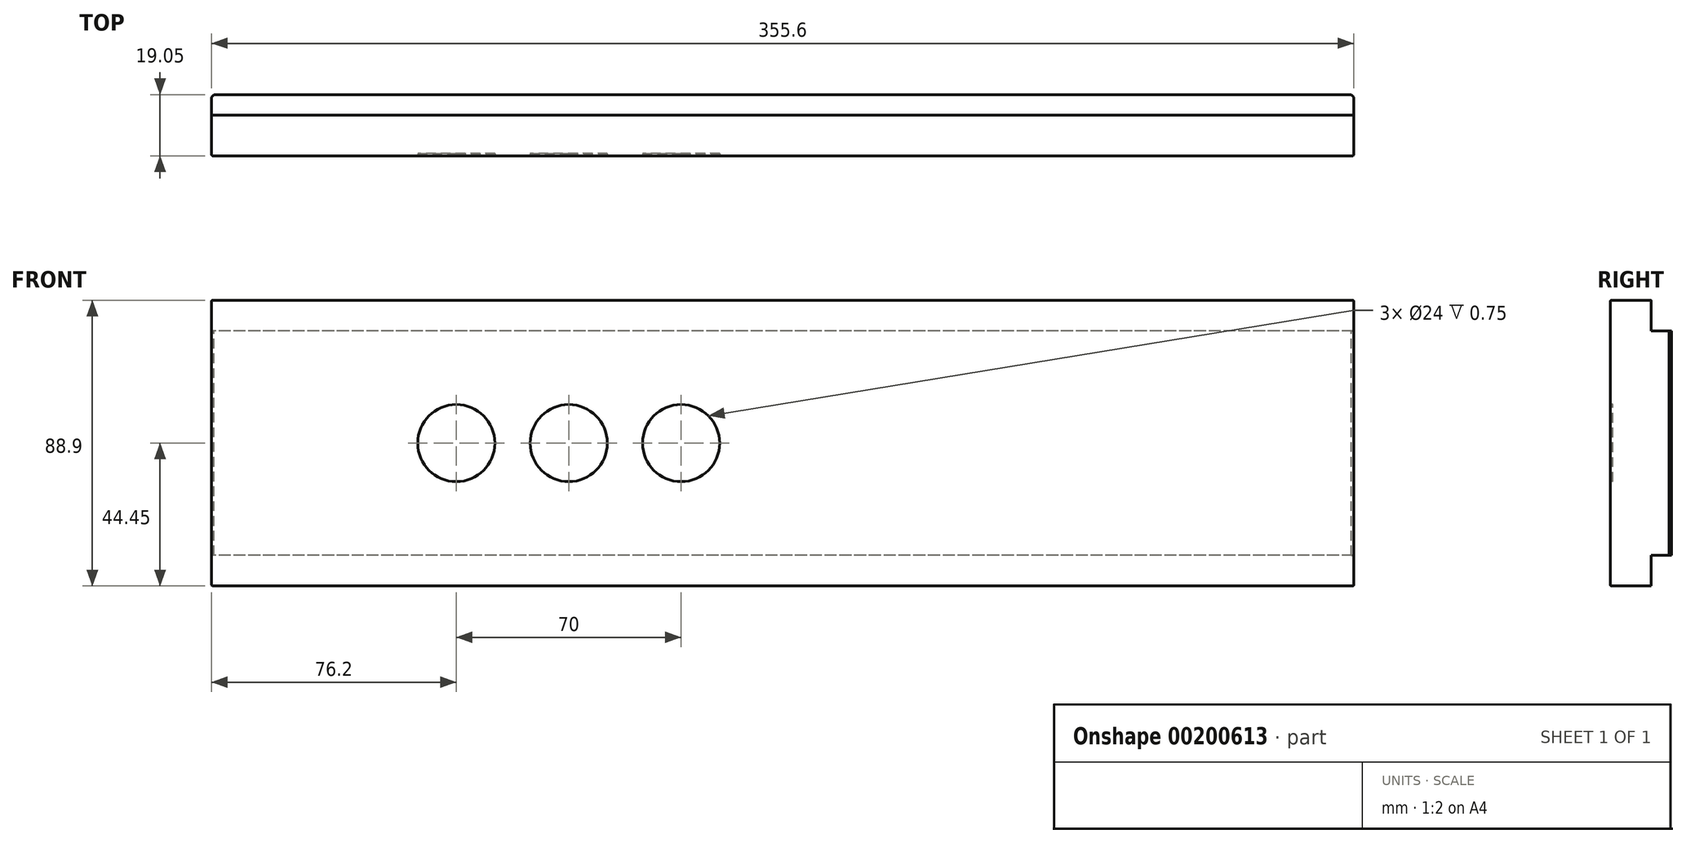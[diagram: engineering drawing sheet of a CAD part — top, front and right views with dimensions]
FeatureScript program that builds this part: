
annotation { "Feature Type Name" : "Feature", "Feature Type Description" : "" }
export const myFeature = defineFeature(function(context is Context, id is Id, definition is map)
    precondition{}
    {
        {
            assignVariable(context, id + "F0", {"name" : "width", "anyValue" : 0.75});
        }
        {
            var Q0;
            Q0=qCreatedBy(makeId("Right.planeOp"),FACE);
            var sketch = newSketch(context, id + "F1", { "sketchPlane" : qUnion([Q0])});
            skLineSegment(sketch, "E0.top", {"start": v(-6.35, 34.93) * mm, "end": v(0, 34.93) * mm});
            skLineSegment(sketch, "E0.left", {"start": v(-6.35, 44.45) * mm, "end": v(-6.35, 34.93) * mm});
            skLineSegment(sketch, "E1.bottom", {"start": v(0, 0) * mm, "end": v(-19.05, 0) * mm});
            skLineSegment(sketch, "E2", {"start": v(-19.05, 44.45) * mm, "end": v(-19.05, 0) * mm});
            skLineSegment(sketch, "E3", {"start": v(-19.05, 44.45) * mm, "end": v(-6.35, 44.45) * mm});
            skLineSegment(sketch, "E4", {"start": v(0, 34.93) * mm, "end": v(0, 0) * mm});
            skSolve(sketch);
        }
        {
            var Q0;
            Q0=makeQuery(id+"F1.imprint","IMPRINT",FACE,{"disambiguationData":[TD([[makeQuery(id+"F1.imprint","IMPRINT",EDGE,{"derivedFrom":sQuery(id+"F1.wireOp",EDGE,"E0.top")}),-1.0]])]});
            var Q1;
            Q1=makeQuery(id+"F1.imprint","IMPRINT",FACE,{"disambiguationData":[TD([[makeQuery(id+"F1.imprint","IMPRINT",EDGE,{"derivedFrom":sQuery(id+"F1.wireOp",EDGE,"E1.bottom")}),1.0]])]});
            extrude(context, id + "F2", {"entities" : qUnion([Q0, Q1]), "depth" : 177.8 * mm});
        }
        {
            var Q0;
            {var subQ0=makeQuery(id+"F4.opChamfer","BLEND_EDGE",EDGE,{"blendedFrom":[makeQuery(id+"F2.opExtrude","CAP_EDGE",EDGE,{"disambiguationData":[OSD([sQuery(id+"F1.wireOp",EDGE,"E4")])],"isStart":true}),makeQuery(id+"F2.opExtrude","SWEPT_FACE",FACE,{"disambiguationData":[OSD([sQuery(id+"F1.wireOp",EDGE,"E2")])]})],"blendedInto":[makeQuery(id+"F2.opExtrude","SWEPT_FACE",FACE,{"disambiguationData":[OSD([sQuery(id+"F1.wireOp",EDGE,"E2")])]})]});Q0=makeQuery(id+"F7.boolean.opBoolean","MERGE",EDGE,{"derivedFrom":[subQ0,makeQuery(id+"F7.opPattern","COPY",EDGE,{"derivedFrom":subQ0,"instanceName":"1"})]});}
            var Q1;
            Q1=makeQuery(id+"F2.opExtrude","CAP_EDGE",EDGE,{"disambiguationData":[OSD([sQuery(id+"F1.wireOp",EDGE,"E2")])],"isStart":true});
            fillet(context, id + "F3", {"entities" : qUnion([Q0, Q1]), "radius" : (getVariable(context, 'width') / 2) * mm, "tangentPropagation" : true, "allowEdgeOverflow" : false});
        }
        {
            var Q0;
            Q0=makeQuery(id+"F2.opExtrude","CAP_EDGE",EDGE,{"disambiguationData":[OSD([sQuery(id+"F1.wireOp",EDGE,"E4"),sQuery(id+"F1.wireOp",EDGE,"06acdf28-0093-4394-9228-6f8524038c1c4.MirrorCS")])],"isStart":true});
            chamfer(context, id + "F4", {"entities" : qUnion([Q0]), "width" : (getVariable(context, 'width')) * mm, "tangentPropagation" : true});
        }
        {
            var Q0;
            Q0=makeQuery(id+"F2.opExtrude","SWEPT_BODY",BODY,{"disambiguationData":[OSD([sQuery(id+"F1.wireOp",EDGE,"E0.top"),sQuery(id+"F1.wireOp",EDGE,"E0.left"),sQuery(id+"F1.wireOp",EDGE,"E2"),sQuery(id+"F1.wireOp",EDGE,"E3"),sQuery(id+"F1.wireOp",EDGE,"E4"),sQuery(id+"F1.wireOp",EDGE,"06acdf28-0093-4394-9228-6f8524038c1c0.MirrorCS"),sQuery(id+"F1.wireOp",EDGE,"06acdf28-0093-4394-9228-6f8524038c1c1.MirrorCS"),sQuery(id+"F1.wireOp",EDGE,"06acdf28-0093-4394-9228-6f8524038c1c2.MirrorCS"),sQuery(id+"F1.wireOp",EDGE,"06acdf28-0093-4394-9228-6f8524038c1c3.MirrorCS"),sQuery(id+"F1.wireOp",EDGE,"06acdf28-0093-4394-9228-6f8524038c1c4.MirrorCS")])]});
            var Q1;
            Q1=makeQuery(id+"F2.opExtrude","CAP_FACE",FACE,{"disambiguationData":[OSD([sQuery(id+"F1.wireOp",EDGE,"E0.top"),sQuery(id+"F1.wireOp",EDGE,"E0.left"),sQuery(id+"F1.wireOp",EDGE,"E2"),sQuery(id+"F1.wireOp",EDGE,"E3"),sQuery(id+"F1.wireOp",EDGE,"E4"),sQuery(id+"F1.wireOp",EDGE,"06acdf28-0093-4394-9228-6f8524038c1c0.MirrorCS"),sQuery(id+"F1.wireOp",EDGE,"06acdf28-0093-4394-9228-6f8524038c1c1.MirrorCS"),sQuery(id+"F1.wireOp",EDGE,"06acdf28-0093-4394-9228-6f8524038c1c2.MirrorCS"),sQuery(id+"F1.wireOp",EDGE,"06acdf28-0093-4394-9228-6f8524038c1c3.MirrorCS"),sQuery(id+"F1.wireOp",EDGE,"06acdf28-0093-4394-9228-6f8524038c1c4.MirrorCS")])],"isStart":false});
            mirror(context, id + "F5", {"operationType" : NewBodyOperationType.ADD, "entities" : qUnion([Q0]), "mirrorPlane" : qUnion([Q1])});
        }
        {
            var Q0;
            {var subQ0=makeQuery(id+"F2.opExtrude","SWEPT_EDGE",EDGE,{"disambiguationData":[OSD([sQuery(id+"F1.wireOp",EDGE,"E2"),sQuery(id+"F1.wireOp",EDGE,"E3")])]});Q0=makeQuery(id+"F5.boolean.opBoolean","MERGE",EDGE,{"derivedFrom":[subQ0,makeQuery(id+"F5.opPattern","COPY",EDGE,{"derivedFrom":subQ0,"instanceName":"1"})]});}
            fillet(context, id + "F6", {"entities" : qUnion([Q0]), "radius" : (getVariable(context, 'width') / 2) * mm, "tangentPropagation" : true, "allowEdgeOverflow" : false});
        }
        {
            var Q0;
            Q0=makeQuery(id+"F2.opExtrude","SWEPT_BODY",BODY,{"disambiguationData":[OSD([sQuery(id+"F1.wireOp",EDGE,"E0.top"),sQuery(id+"F1.wireOp",EDGE,"E0.left"),sQuery(id+"F1.wireOp",EDGE,"E1.bottom"),sQuery(id+"F1.wireOp",EDGE,"E2"),sQuery(id+"F1.wireOp",EDGE,"E3"),sQuery(id+"F1.wireOp",EDGE,"E4")])]});
            var Q1;
            {var subQ0=makeQuery(id+"F2.opExtrude","SWEPT_FACE",FACE,{"disambiguationData":[OSD([sQuery(id+"F1.wireOp",EDGE,"E1.bottom")])]});Q1=makeQuery(id+"F5.boolean.opBoolean","MERGE",FACE,{"derivedFrom":[subQ0,makeQuery(id+"F5.opPattern","COPY",FACE,{"derivedFrom":subQ0,"instanceName":"1"})]});}
            mirror(context, id + "F7", {"operationType" : NewBodyOperationType.ADD, "entities" : qUnion([Q0]), "mirrorPlane" : qUnion([Q1])});
        }
        {
            var Q0;
            {var subQ0=makeQuery(id+"F2.opExtrude","SWEPT_FACE",FACE,{"disambiguationData":[OSD([sQuery(id+"F1.wireOp",EDGE,"E2")])]});var subQ1=makeQuery(id+"F5.boolean.opBoolean","MERGE",FACE,{"derivedFrom":[subQ0,makeQuery(id+"F5.opPattern","COPY",FACE,{"derivedFrom":subQ0,"instanceName":"1"})]});Q0=makeQuery(id+"F7.boolean.opBoolean","MERGE",FACE,{"derivedFrom":[subQ1,makeQuery(id+"F7.opPattern","COPY",FACE,{"derivedFrom":subQ1,"instanceName":"1"})]});}
            var sketch = newSketch(context, id + "F8", { "sketchPlane" : qUnion([Q0])});
            skCircle(sketch, "E5", {"center": v(76.2, 0) * mm, "radius": 12 * mm});
            skCircle(sketch, "E6", {"center": v(111.2, 0) * mm, "radius": 12 * mm});
            skCircle(sketch, "E7", {"center": v(146.2, 0) * mm, "radius": 12 * mm});
            skSolve(sketch);
        }
        {
            var Q0;
            Q0=makeQuery(id+"F8.imprint","IMPRINT",FACE,{"disambiguationData":[TD([[makeQuery(id+"F8.imprint","IMPRINT",EDGE,{"derivedFrom":sQuery(id+"F8.wireOp",EDGE,"E5")}),1.0]])]});
            var Q1;
            Q1=makeQuery(id+"F8.imprint","IMPRINT",FACE,{"disambiguationData":[TD([[makeQuery(id+"F8.imprint","IMPRINT",EDGE,{"derivedFrom":sQuery(id+"F8.wireOp",EDGE,"E6")}),1.0]])]});
            var Q2;
            Q2=makeQuery(id+"F8.imprint","IMPRINT",FACE,{"disambiguationData":[TD([[makeQuery(id+"F8.imprint","IMPRINT",EDGE,{"derivedFrom":sQuery(id+"F8.wireOp",EDGE,"E7")}),1.0]])]});
            extrude(context, id + "F9", {"entities" : qUnion([Q0, Q1, Q2]), "operationType" : NewBodyOperationType.REMOVE, "oppositeDirection" : true, "depth" : (getVariable(context, 'width')) * mm});
        }
        {
            var Q0;
            {var subQ0=makeQuery(id+"F2.opExtrude","SWEPT_FACE",FACE,{"disambiguationData":[OSD([sQuery(id+"F1.wireOp",EDGE,"E4")])]});var subQ1=makeQuery(id+"F5.boolean.opBoolean","MERGE",FACE,{"derivedFrom":[subQ0,makeQuery(id+"F5.opPattern","COPY",FACE,{"derivedFrom":subQ0,"instanceName":"1"})]});Q0=makeQuery(id+"F7.boolean.opBoolean","MERGE",FACE,{"derivedFrom":[subQ1,makeQuery(id+"F7.opPattern","COPY",FACE,{"derivedFrom":subQ1,"instanceName":"1"})]});}
            var sketch = newSketch(context, id + "F10", { "sketchPlane" : qUnion([Q0])});
            skCircle(sketch, "E8", {"center": v(-146.2, 0) * mm, "radius": 15 * mm});
            skCircle(sketch, "E9", {"center": v(-111.2, 0) * mm, "radius": 15 * mm});
            skCircle(sketch, "E10", {"center": v(-76.2, 0) * mm, "radius": 15 * mm});
            skSolve(sketch);
        }
        {
            var Q0;
            Q0=makeQuery(id+"F10.imprint","IMPRINT",FACE,{"disambiguationData":[TD([[makeQuery(id+"F10.imprint","IMPRINT",EDGE,{"derivedFrom":sQuery(id+"F10.wireOp",EDGE,"E8")}),1.0]])]});
            var Q1;
            Q1=makeQuery(id+"F10.imprint","IMPRINT",FACE,{"disambiguationData":[TD([[makeQuery(id+"F10.imprint","IMPRINT",EDGE,{"derivedFrom":sQuery(id+"F10.wireOp",EDGE,"E9")}),1.0]])]});
            var Q2;
            Q2=makeQuery(id+"F10.imprint","IMPRINT",FACE,{"disambiguationData":[TD([[makeQuery(id+"F10.imprint","IMPRINT",EDGE,{"derivedFrom":sQuery(id+"F10.wireOp",EDGE,"E10")}),1.0]])]});
            extrude(context, id + "F11", {"entities" : qUnion([Q0, Q1, Q2]), "operationType" : NewBodyOperationType.REMOVE, "oppositeDirection" : true, "depth" : (getVariable(context, 'width') * mm) - 8 * mm});
        }
    });
